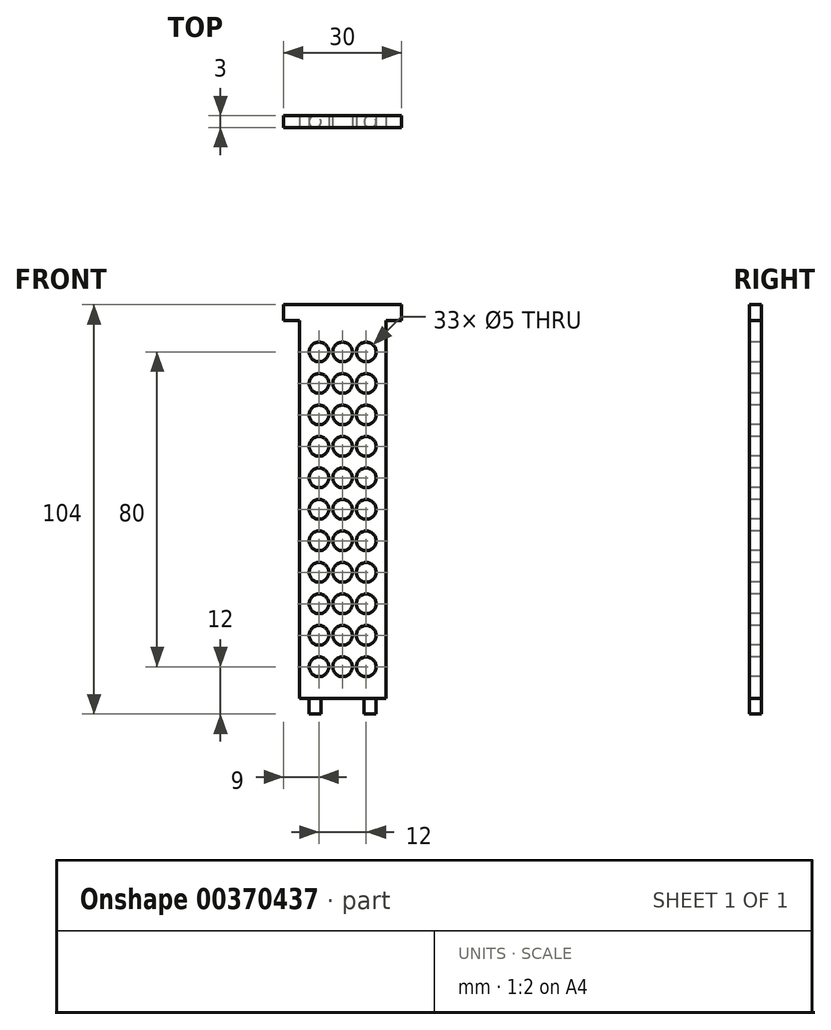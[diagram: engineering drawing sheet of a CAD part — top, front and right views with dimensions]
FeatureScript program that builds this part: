
annotation { "Feature Type Name" : "Feature", "Feature Type Description" : "" }
export const myFeature = defineFeature(function(context is Context, id is Id, definition is map)
    precondition{}
    {
        {
            var Q0;
            Q0=qCreatedBy(makeId("Top.planeOp"),FACE);
            var sketch = newSketch(context, id + "F0", { "sketchPlane" : qUnion([Q0])});
            skLineSegment(sketch, "E0.bottom", {"start": v(0, 0) * mm, "end": v(22, 0) * mm});
            skLineSegment(sketch, "E0.top", {"start": v(0, -3) * mm, "end": v(22, -3) * mm});
            skLineSegment(sketch, "E0.left", {"start": v(0, 0) * mm, "end": v(0, -3) * mm});
            skLineSegment(sketch, "E0.right", {"start": v(22, 0) * mm, "end": v(22, -3) * mm});
            skSolve(sketch);
        }
        {
            var Q0;
            Q0=makeQuery(id+"F0.imprint","IMPRINT",FACE,{"disambiguationData":[TD([[makeQuery(id+"F0.imprint","IMPRINT",EDGE,{"derivedFrom":sQuery(id+"F0.wireOp",EDGE,"E0.bottom")}),-1.0]])]});
            extrude(context, id + "F1", {"entities" : qUnion([Q0]), "depth" : 100 * mm});
        }
        {
            var Q0;
            Q0=makeQuery(id+"F1.opExtrude","CAP_FACE",FACE,{"disambiguationData":[OSD([sQuery(id+"F0.wireOp",EDGE,"E0.bottom"),sQuery(id+"F0.wireOp",EDGE,"E0.top"),sQuery(id+"F0.wireOp",EDGE,"E0.left"),sQuery(id+"F0.wireOp",EDGE,"E0.right")])],"isStart":true});
            var sketch = newSketch(context, id + "F2", { "sketchPlane" : qUnion([Q0])});
            skCircle(sketch, "E1", {"center": v(4, 1.5) * mm, "radius": 1.5 * mm});
            skCircle(sketch, "E2", {"center": v(18, 1.5) * mm, "radius": 1.5 * mm});
            skSolve(sketch);
        }
        {
            var Q0;
            {var subQ0=sQuery(id+"F2.wireOp",EDGE,"E1");var subQ1=makeQuery(id+"F2.imprint","INTERSECT",VERTEX,{"derivedFrom":[makeQuery(id+"F1.opExtrude","CAP_EDGE",EDGE,{"disambiguationData":[OSD([sQuery(id+"F0.wireOp",EDGE,"E0.bottom")])],"isStart":true}),subQ0]});Q0=makeQuery(id+"F2.imprint","IMPRINT",FACE,{"disambiguationData":[TD([[makeQuery(id+"F2.imprint","IMPRINT",EDGE,{"disambiguationData":[TD([[subQ1,1.0]])],"derivedFrom":subQ0}),1.0]])]});}
            var Q1;
            {var subQ0=sQuery(id+"F2.wireOp",EDGE,"E2");var subQ1=makeQuery(id+"F2.imprint","INTERSECT",VERTEX,{"derivedFrom":[makeQuery(id+"F1.opExtrude","CAP_EDGE",EDGE,{"disambiguationData":[OSD([sQuery(id+"F0.wireOp",EDGE,"E0.bottom")])],"isStart":true}),subQ0]});Q1=makeQuery(id+"F2.imprint","IMPRINT",FACE,{"disambiguationData":[TD([[makeQuery(id+"F2.imprint","IMPRINT",EDGE,{"disambiguationData":[TD([[subQ1,1.0]])],"derivedFrom":subQ0}),1.0]])]});}
            extrude(context, id + "F3", {"entities" : qUnion([Q0, Q1]), "operationType" : NewBodyOperationType.ADD, "depth" : 4 * mm});
        }
        {
            var Q0;
            Q0=makeQuery(id+"F1.opExtrude","CAP_FACE",FACE,{"disambiguationData":[OSD([sQuery(id+"F0.wireOp",EDGE,"E0.bottom"),sQuery(id+"F0.wireOp",EDGE,"E0.top"),sQuery(id+"F0.wireOp",EDGE,"E0.left"),sQuery(id+"F0.wireOp",EDGE,"E0.right")])],"isStart":false});
            var sketch = newSketch(context, id + "F4", { "sketchPlane" : qUnion([Q0])});
            skLineSegment(sketch, "E3.bottom", {"start": v(-4, 0) * mm, "end": v(26, 0) * mm});
            skLineSegment(sketch, "E3.top", {"start": v(-4, -3) * mm, "end": v(26, -3) * mm});
            skLineSegment(sketch, "E3.left", {"start": v(-4, 0) * mm, "end": v(-4, -3) * mm});
            skLineSegment(sketch, "E3.right", {"start": v(26, 0) * mm, "end": v(26, -3) * mm});
            skSolve(sketch);
        }
        {
            var Q0;
            {var subQ2=sQuery(id+"F4.wireOp",EDGE,"E3.left");Q0=makeQuery(id+"F4.imprint","IMPRINT",FACE,{"disambiguationData":[TD([[makeQuery(id+"F4.imprint","IMPRINT",EDGE,{"derivedFrom":subQ2}),1.0]])]});}
            var Q1;
            {var subQ2=sQuery(id+"F4.wireOp",EDGE,"E3.right");Q1=makeQuery(id+"F4.imprint","IMPRINT",FACE,{"disambiguationData":[TD([[makeQuery(id+"F4.imprint","IMPRINT",EDGE,{"derivedFrom":subQ2}),-1.0]])]});}
            var Q2;
            {var subQ1=makeQuery(id+"F1.opExtrude","CAP_EDGE",EDGE,{"disambiguationData":[OSD([sQuery(id+"F0.wireOp",EDGE,"E0.left")])],"isStart":false});Q2=makeQuery(id+"F4.imprint","IMPRINT",FACE,{"disambiguationData":[TD([[makeQuery(id+"F4.imprint","IMPRINT",EDGE,{"derivedFrom":subQ1}),1.0]])]});}
            extrude(context, id + "F5", {"entities" : qUnion([Q0, Q1, Q2]), "operationType" : NewBodyOperationType.ADD, "oppositeDirection" : true, "depth" : 4 * mm});
        }
        {
            var Q0;
            Q0=makeQuery(id+"F5.boolean.opBoolean","MERGE",FACE,{"derivedFrom":[makeQuery(id+"F1.opExtrude","SWEPT_FACE",FACE,{"disambiguationData":[OSD([sQuery(id+"F0.wireOp",EDGE,"E0.top")])]}),makeQuery(id+"F5.opExtrude","SWEPT_FACE",FACE,{"disambiguationData":[OSD([sQuery(id+"F4.wireOp",EDGE,"E3.top")])]})]});
            var sketch = newSketch(context, id + "F6", { "sketchPlane" : qUnion([Q0])});
            skCircle(sketch, "E4", {"center": v(5, 8) * mm, "radius": 2.5 * mm});
            skCircle(sketch, "E5.1.0.0", {"center": v(11, 8) * mm, "radius": 2.5 * mm});
            skCircle(sketch, "E5.2.0.0", {"center": v(17, 8) * mm, "radius": 2.5 * mm});
            skLineSegment(sketch, "E5.direction1", {"start": v(5, 8) * mm, "end": v(11, 8) * mm, "construction": true});
            skCircle(sketch, "E6.0.1.0", {"center": v(5, 16) * mm, "radius": 2.5 * mm});
            skCircle(sketch, "E6.0.1.1", {"center": v(11, 16) * mm, "radius": 2.5 * mm});
            skCircle(sketch, "E6.0.1.2", {"center": v(17, 16) * mm, "radius": 2.5 * mm});
            skCircle(sketch, "E6.0.2.0", {"center": v(5, 24) * mm, "radius": 2.5 * mm});
            skCircle(sketch, "E6.0.2.1", {"center": v(11, 24) * mm, "radius": 2.5 * mm});
            skCircle(sketch, "E6.0.2.2", {"center": v(17, 24) * mm, "radius": 2.5 * mm});
            skCircle(sketch, "E6.0.3.0", {"center": v(5, 32) * mm, "radius": 2.5 * mm});
            skCircle(sketch, "E6.0.3.1", {"center": v(11, 32) * mm, "radius": 2.5 * mm});
            skCircle(sketch, "E6.0.3.2", {"center": v(17, 32) * mm, "radius": 2.5 * mm});
            skCircle(sketch, "E6.0.4.0", {"center": v(5, 40) * mm, "radius": 2.5 * mm});
            skCircle(sketch, "E6.0.4.1", {"center": v(11, 40) * mm, "radius": 2.5 * mm});
            skCircle(sketch, "E6.0.4.2", {"center": v(17, 40) * mm, "radius": 2.5 * mm});
            skCircle(sketch, "E6.0.5.0", {"center": v(5, 48) * mm, "radius": 2.5 * mm});
            skCircle(sketch, "E6.0.5.1", {"center": v(11, 48) * mm, "radius": 2.5 * mm});
            skCircle(sketch, "E6.0.5.2", {"center": v(17, 48) * mm, "radius": 2.5 * mm});
            skCircle(sketch, "E6.0.6.0", {"center": v(5, 56) * mm, "radius": 2.5 * mm});
            skCircle(sketch, "E6.0.6.1", {"center": v(11, 56) * mm, "radius": 2.5 * mm});
            skCircle(sketch, "E6.0.6.2", {"center": v(17, 56) * mm, "radius": 2.5 * mm});
            skCircle(sketch, "E6.0.7.0", {"center": v(5, 64) * mm, "radius": 2.5 * mm});
            skCircle(sketch, "E6.0.7.1", {"center": v(11, 64) * mm, "radius": 2.5 * mm});
            skCircle(sketch, "E6.0.7.2", {"center": v(17, 64) * mm, "radius": 2.5 * mm});
            skCircle(sketch, "E6.0.8.0", {"center": v(5, 72) * mm, "radius": 2.5 * mm});
            skCircle(sketch, "E6.0.8.1", {"center": v(11, 72) * mm, "radius": 2.5 * mm});
            skCircle(sketch, "E6.0.8.2", {"center": v(17, 72) * mm, "radius": 2.5 * mm});
            skCircle(sketch, "E6.0.9.0", {"center": v(5, 80) * mm, "radius": 2.5 * mm});
            skCircle(sketch, "E6.0.9.1", {"center": v(11, 80) * mm, "radius": 2.5 * mm});
            skCircle(sketch, "E6.0.9.2", {"center": v(17, 80) * mm, "radius": 2.5 * mm});
            skCircle(sketch, "E6.0.10.0", {"center": v(5, 88) * mm, "radius": 2.5 * mm});
            skCircle(sketch, "E6.0.10.1", {"center": v(11, 88) * mm, "radius": 2.5 * mm});
            skCircle(sketch, "E6.0.10.2", {"center": v(17, 88) * mm, "radius": 2.5 * mm});
            skLineSegment(sketch, "E6.direction1", {"start": v(5, 8) * mm, "end": v(30, 8) * mm, "construction": true});
            skLineSegment(sketch, "E6.direction2", {"start": v(5, 8) * mm, "end": v(5, 16) * mm, "construction": true});
            skSolve(sketch);
        }
        {
            var Q0;
            Q0 = qSketchRegion(id + "F6", true);
            extrude(context, id + "F7", {"entities" : qUnion([Q0]), "operationType" : NewBodyOperationType.REMOVE, "oppositeDirection" : true, "depth" : 25 * mm});
        }
    });
